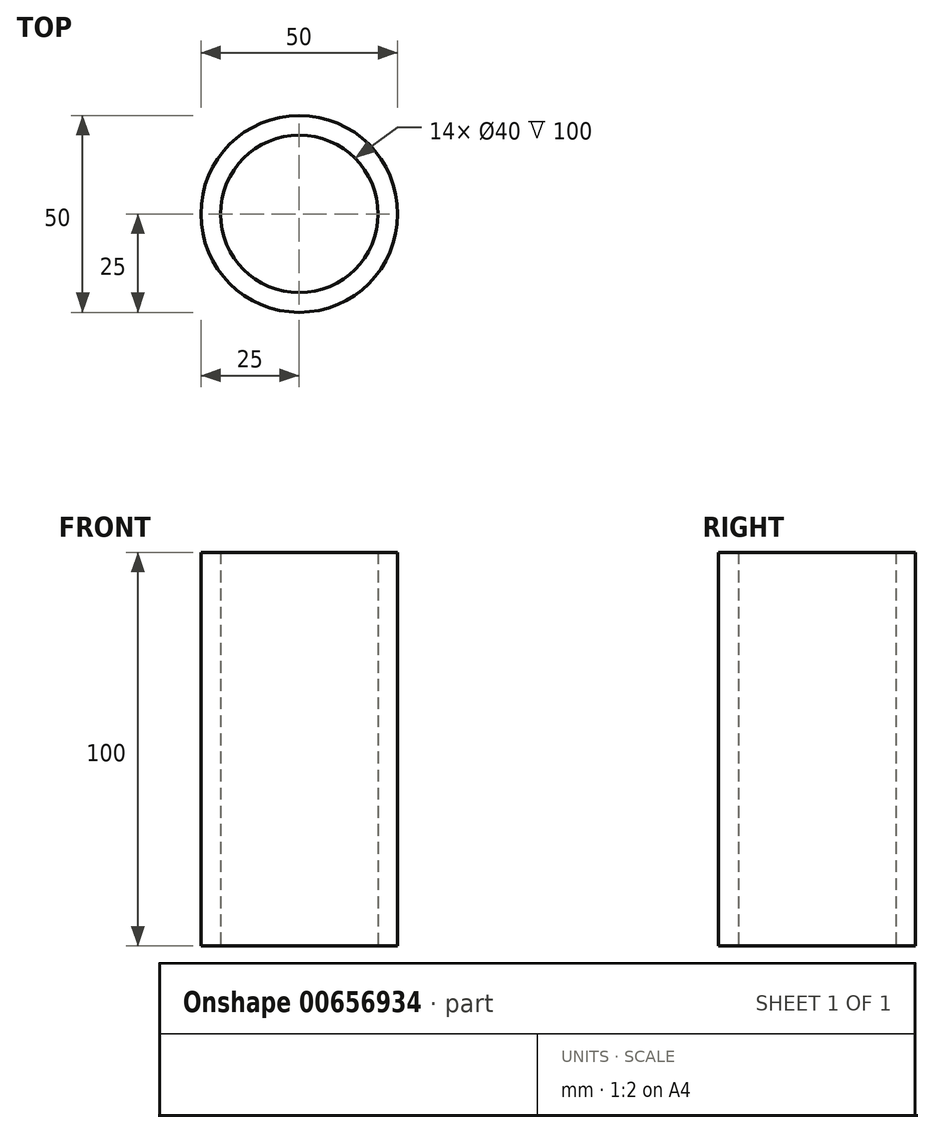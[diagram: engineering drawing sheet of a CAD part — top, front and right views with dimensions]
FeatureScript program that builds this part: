
annotation { "Feature Type Name" : "Feature", "Feature Type Description" : "" }
export const myFeature = defineFeature(function(context is Context, id is Id, definition is map)
    precondition{}
    {
        {
            var Q0;
            Q0=qCreatedBy(makeId("Top.planeOp"),FACE);
            var sketch = newSketch(context, id + "F0", { "sketchPlane" : qUnion([Q0])});
            skCircle(sketch, "E0", {"center": v(0, 0) * mm, "radius": 25 * mm});
            skCircle(sketch, "E1", {"center": v(0, 0) * mm, "radius": 20 * mm});
            skSolve(sketch);
        }
        {
            var Q0;
            Q0=makeQuery(id+"F0.imprint","IMPRINT",FACE,{"disambiguationData":[TD([[makeQuery(id+"F0.imprint","IMPRINT",EDGE,{"derivedFrom":sQuery(id+"F0.wireOp",EDGE,"E0")}),1.0]])]});
            var Q1;
            Q1 = qConstructionFilter(qBodyType(qCreatedBy(id + "F0" ,EDGE), BodyType.WIRE), ConstructionObject.NO);
            extrude(context, id + "F1", {"entities" : qUnion([Q0]), "surfaceEntities" : qUnion([Q1]), "depth" : 100 * mm, "offsetDistance" : 25 * mm});
        }
    });
